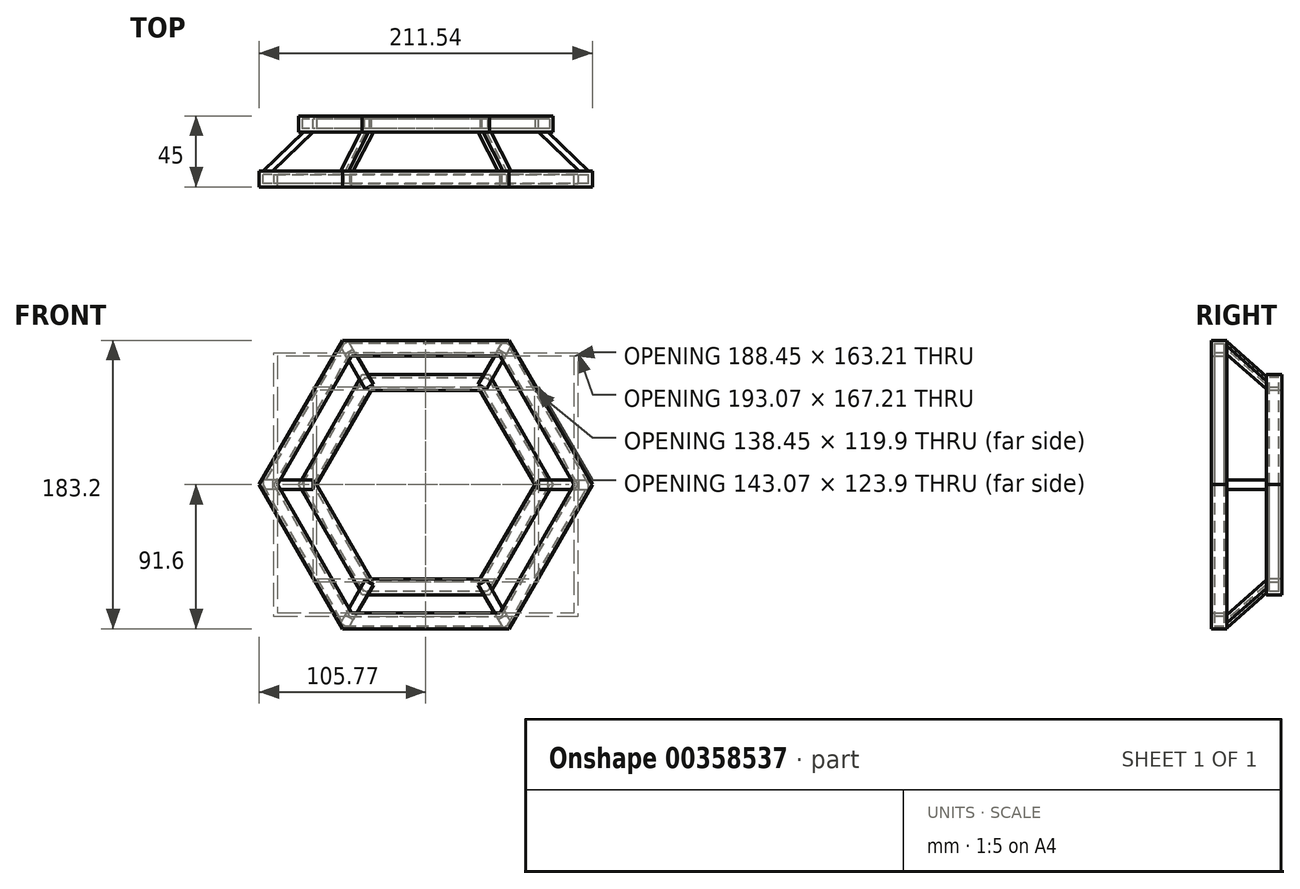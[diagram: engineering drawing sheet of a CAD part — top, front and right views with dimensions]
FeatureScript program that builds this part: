
annotation { "Feature Type Name" : "Feature", "Feature Type Description" : "" }
export const myFeature = defineFeature(function(context is Context, id is Id, definition is map)
    precondition{}
    {
        {
            var Q0;
            Q0=qCreatedBy(makeId("Front.planeOp"),FACE);
            var sketch = newSketch(context, id + "F0", { "sketchPlane" : qUnion([Q0])});
            skCircle(sketch, "E0.cCircle", {"center": v(0, 0) * mm, "radius": 86.6 * mm, "construction": true});
            skLineSegment(sketch, "E0.0", {"start": v(-50, 86.6) * mm, "end": v(50, 86.6) * mm});
            skLineSegment(sketch, "E0.1", {"start": v(50, 86.6) * mm, "end": v(100, 0) * mm});
            skLineSegment(sketch, "E0.2", {"start": v(100, 0) * mm, "end": v(50, -86.6) * mm});
            skLineSegment(sketch, "E0.3", {"start": v(50, -86.6) * mm, "end": v(-50, -86.6) * mm});
            skLineSegment(sketch, "E0.4", {"start": v(-50, -86.6) * mm, "end": v(-100, 0) * mm});
            skLineSegment(sketch, "E0.5", {"start": v(-100, 0) * mm, "end": v(-50, 86.6) * mm});
            skPoint(sketch, "E0.0.midPoint", {"position": v(0, 86.6) * mm});
            skSolve(sketch);
        }
        {
            var Q0;
            Q0=qCreatedBy(makeId("Right.planeOp"),FACE);
            var sketch = newSketch(context, id + "F1", { "sketchPlane" : qUnion([Q0])});
            skLineSegment(sketch, "E1.bottom", {"start": v(-5, -81.6) * mm, "end": v(5, -81.6) * mm});
            skLineSegment(sketch, "E1.top", {"start": v(-5, -91.6) * mm, "end": v(5, -91.6) * mm});
            skLineSegment(sketch, "E1.left", {"start": v(-5, -81.6) * mm, "end": v(-5, -91.6) * mm});
            skLineSegment(sketch, "E1.right", {"start": v(5, -81.6) * mm, "end": v(5, -91.6) * mm});
            skPoint(sketch, "E1.middle", {"position": v(0, -86.6) * mm});
            skLineSegment(sketch, "E2.bottom", {"start": v(-3, -83.6) * mm, "end": v(3, -83.6) * mm});
            skLineSegment(sketch, "E2.top", {"start": v(-3, -89.6) * mm, "end": v(3, -89.6) * mm});
            skLineSegment(sketch, "E2.left", {"start": v(-3, -83.6) * mm, "end": v(-3, -89.6) * mm});
            skLineSegment(sketch, "E2.right", {"start": v(3, -83.6) * mm, "end": v(3, -89.6) * mm});
            skSolve(sketch);
        }
        {
            var Q0;
            Q0=makeQuery(id+"F1.imprint","IMPRINT",FACE,{"disambiguationData":[TD([[makeQuery(id+"F1.imprint","IMPRINT",EDGE,{"derivedFrom":sQuery(id+"F1.wireOp",EDGE,"E1.bottom")}),-1.0]])]});
            var Q1;
            Q1=sQuery(id+"F0.wireOp",EDGE,"E0.3");
            var Q2;
            Q2=sQuery(id+"F0.wireOp",EDGE,"E0.4");
            var Q3;
            Q3=sQuery(id+"F0.wireOp",EDGE,"E0.5");
            var Q4;
            Q4=sQuery(id+"F0.wireOp",EDGE,"E0.0");
            var Q5;
            Q5=sQuery(id+"F0.wireOp",EDGE,"E0.1");
            var Q6;
            Q6=sQuery(id+"F0.wireOp",EDGE,"E0.2");
            sweep(context, id + "F2", {"profiles" : qUnion([Q0]), "path" : qUnion([Q1, Q2, Q3, Q4, Q5, Q6])});
        }
        {
            var Q0;
            Q0=qCreatedBy(makeId("Front.planeOp"),FACE);
            cPlane(context, id + "F3", {"entities" : qUnion([Q0]), "cplaneType" : CPlaneType.OFFSET, "offset" : 35 * mm, "oppositeDirection" : true, "width" : 150 * mm, "height" : 150 * mm});
        }
        {
            var Q0;
            Q0=qCreatedBy(id+"F3.planeOp",FACE);
            var sketch = newSketch(context, id + "F4", { "sketchPlane" : qUnion([Q0])});
            skCircle(sketch, "E3.cCircle", {"center": v(0, 0) * mm, "radius": 64.95 * mm, "construction": true});
            skLineSegment(sketch, "E3.0", {"start": v(37.5, 64.95) * mm, "end": v(75, 0) * mm});
            skLineSegment(sketch, "E3.1", {"start": v(75, 0) * mm, "end": v(37.5, -64.95) * mm});
            skLineSegment(sketch, "E3.2", {"start": v(37.5, -64.95) * mm, "end": v(-37.5, -64.95) * mm});
            skLineSegment(sketch, "E3.3", {"start": v(-37.5, -64.95) * mm, "end": v(-75, 0) * mm});
            skLineSegment(sketch, "E3.4", {"start": v(-75, 0) * mm, "end": v(-37.5, 64.95) * mm});
            skLineSegment(sketch, "E3.5", {"start": v(-37.5, 64.95) * mm, "end": v(37.5, 64.95) * mm});
            skPoint(sketch, "E3.0.midPoint", {"position": v(56.25, 32.48) * mm});
            skSolve(sketch);
        }
        {
            var Q0;
            Q0=qCreatedBy(makeId("Right.planeOp"),FACE);
            var sketch = newSketch(context, id + "F5", { "sketchPlane" : qUnion([Q0])});
            skLineSegment(sketch, "E4.bottom", {"start": v(40, 69.95) * mm, "end": v(30, 69.95) * mm});
            skLineSegment(sketch, "E4.top", {"start": v(40, 59.95) * mm, "end": v(30, 59.95) * mm});
            skLineSegment(sketch, "E4.left", {"start": v(40, 69.95) * mm, "end": v(40, 59.95) * mm});
            skLineSegment(sketch, "E4.right", {"start": v(30, 69.95) * mm, "end": v(30, 59.95) * mm});
            skPoint(sketch, "E4.middle", {"position": v(35, 64.95) * mm});
            skLineSegment(sketch, "E5.bottom", {"start": v(38, 67.95) * mm, "end": v(32, 67.95) * mm});
            skLineSegment(sketch, "E5.top", {"start": v(38, 61.95) * mm, "end": v(32, 61.95) * mm});
            skLineSegment(sketch, "E5.left", {"start": v(38, 67.95) * mm, "end": v(38, 61.95) * mm});
            skLineSegment(sketch, "E5.right", {"start": v(32, 67.95) * mm, "end": v(32, 61.95) * mm});
            skSolve(sketch);
        }
        {
            var Q0;
            Q0=makeQuery(id+"F5.imprint","IMPRINT",FACE,{"disambiguationData":[TD([[makeQuery(id+"F5.imprint","IMPRINT",EDGE,{"derivedFrom":sQuery(id+"F5.wireOp",EDGE,"E4.bottom")}),1.0]])]});
            var Q1;
            Q1=sQuery(id+"F4.wireOp",EDGE,"E3.5");
            var Q2;
            Q2=sQuery(id+"F4.wireOp",EDGE,"E3.0");
            var Q3;
            Q3=sQuery(id+"F4.wireOp",EDGE,"E3.1");
            var Q4;
            Q4=sQuery(id+"F4.wireOp",EDGE,"E3.2");
            var Q5;
            Q5=sQuery(id+"F4.wireOp",EDGE,"E3.3");
            var Q6;
            Q6=sQuery(id+"F4.wireOp",EDGE,"E3.4");
            sweep(context, id + "F6", {"profiles" : qUnion([Q0]), "path" : qUnion([Q1, Q2, Q3, Q4, Q5, Q6])});
        }
        {
            var Q0;
            Q0=qCreatedBy(makeId("Right.planeOp"),FACE);
            var sketch = newSketch(context, id + "F7", { "sketchPlane" : qUnion([Q0])});
            skLineSegment(sketch, "E6", {"start": v(-141.73, 0) * mm, "end": v(143.53, 0) * mm, "construction": true});
            skSolve(sketch);
        }
        {
            var Q0;
            Q0=qCreatedBy(makeId("Top.planeOp"),FACE);
            var sketch = newSketch(context, id + "F8", { "sketchPlane" : qUnion([Q0])});
            skLineSegment(sketch, "E7", {"start": v(-71.73, 30) * mm, "end": v(-97.27, 5) * mm});
            skLineSegment(sketch, "E8", {"start": v(-71.73, 30) * mm, "end": v(-77.73, 30) * mm});
            skLineSegment(sketch, "E9", {"start": v(-77.73, 30) * mm, "end": v(-103.27, 5) * mm});
            skLineSegment(sketch, "E10.0", {"start": v(-97.27, 5) * mm, "end": v(-103.27, 5) * mm});
            skPoint(sketch, "E11.orphan", {"position": v(-52.89, 5) * mm});
            skPoint(sketch, "E12.orphan", {"position": v(-105.77, 5) * mm});
            skSolve(sketch);
        }
        {
            var Q0;
            Q0 = qSketchRegion(id + "F8", true);
            extrude(context, id + "F9", {"entities" : qUnion([Q0]), "endBound" : BoundingType.SYMMETRIC, "depth" : 6 * mm});
        }
        {
            var Q0;
            Q0=makeQuery(id+"F9.opExtrude","SWEPT_BODY",BODY,{"disambiguationData":[OSD([sQuery(id+"F8.wireOp",EDGE,"E7"),sQuery(id+"F8.wireOp",EDGE,"E8"),sQuery(id+"F8.wireOp",EDGE,"E9"),sQuery(id+"F8.wireOp",EDGE,"E10.0")])]});
            var Q1;
            Q1=sQuery(id+"F7.wireOp",EDGE,"E6");
            circularPattern(context, id + "F10", {"entities" : qUnion([Q0]), "axis" : qUnion([Q1]), "angle" : 360 * degree, "instanceCount" : 6, "equalSpace" : true});
        }
    });
